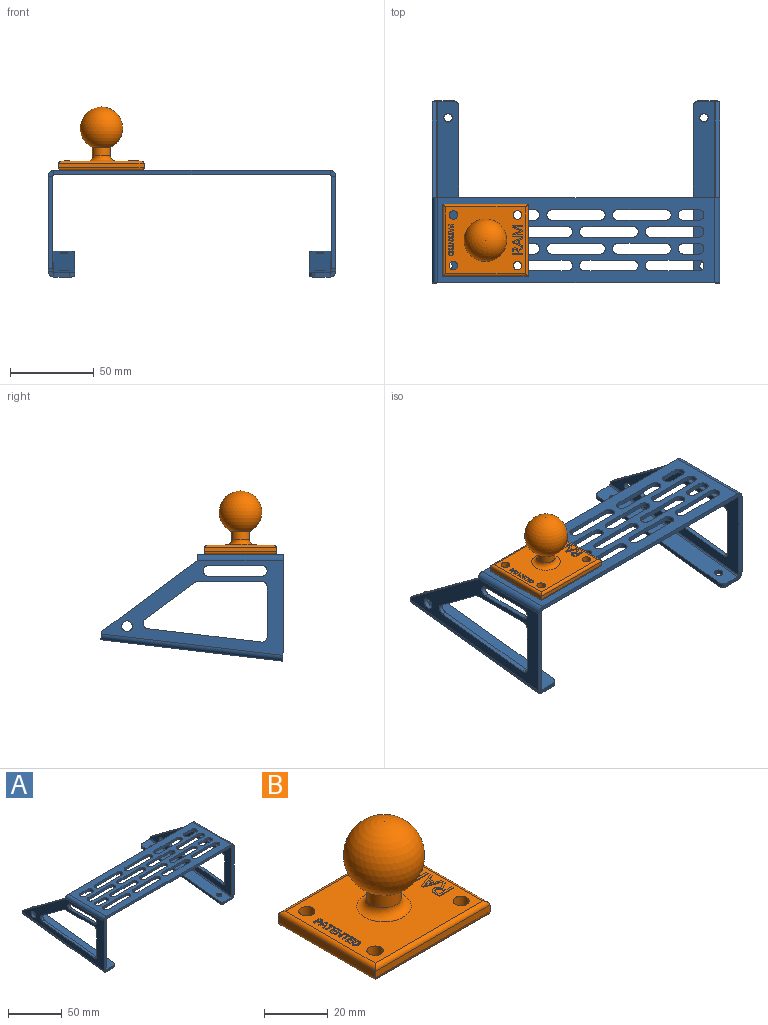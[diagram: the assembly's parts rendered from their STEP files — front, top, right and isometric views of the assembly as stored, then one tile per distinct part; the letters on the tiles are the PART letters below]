
ASSEMBLY  parts=2 mates=1
PART A: 148 faces, bbox 171.5x108.5x63.5 mm
  f0: plane 164.55x2.66mm, normal (0,-1,0), area 437.2mm2, adj f74,f75,f108,f144
  f1: plane 28.58x2.66mm, normal (0,1,0), area 75.9mm2, adj f2,f72,f74,f75
  f2: cylinder r=3.17mm len=6.35mm, axis (0,0,1), area 26.5mm2, adj f1,f3,f74,f75
  f3: plane 28.58x2.66mm, normal (0,-1,0), area 75.9mm2, adj f2,f72,f74,f75
  f4: plane 28.58x2.66mm, normal (0,1,0), area 75.9mm2, adj f5,f71,f74,f75
  f5: cylinder r=3.17mm len=6.35mm, axis (0,0,1), area 26.5mm2, adj f4,f6,f74,f75
  f6: plane 28.58x2.66mm, normal (0,-1,0), area 75.9mm2, adj f5,f71,f74,f75
  f7: plane 28.58x2.66mm, normal (0,1,0), area 75.9mm2, adj f8,f70,f74,f75
  f8: cylinder r=3.17mm len=6.35mm, axis (0,0,1), area 26.5mm2, adj f7,f9,f74,f75
  f9: plane 28.58x2.66mm, normal (0,-1,0), area 75.9mm2, adj f8,f70,f74,f75
  f10: plane 28.58x2.66mm, normal (0,1,0), area 75.9mm2, adj f11,f69,f74,f75
  f11: cylinder r=3.17mm len=6.35mm, axis (0,0,1), area 26.5mm2, adj f10,f12,f74,f75
  f12: plane 28.58x2.66mm, normal (0,-1,0), area 75.9mm2, adj f11,f69,f74,f75
  f13: plane 28.58x2.66mm, normal (0,1,0), area 75.9mm2, adj f14,f68,f74,f75
  f14: cylinder r=3.17mm len=6.35mm, axis (0,0,1), area 26.5mm2, adj f13,f15,f74,f75
  f15: plane 28.58x2.66mm, normal (0,-1,0), area 75.9mm2, adj f14,f68,f74,f75
  f16: plane 28.58x2.66mm, normal (0,1,0), area 75.9mm2, adj f17,f67,f74,f75
  f17: cylinder r=3.17mm len=6.35mm, axis (0,0,1), area 26.5mm2, adj f16,f18,f74,f75
  f18: plane 28.58x2.66mm, normal (0,-1,0), area 75.9mm2, adj f17,f67,f74,f75
  f19: plane 28.58x2.66mm, normal (0,1,0), area 75.9mm2, adj f20,f66,f74,f75
  f20: cylinder r=3.17mm len=6.35mm, axis (0,0,1), area 26.5mm2, adj f19,f21,f74,f75
  f21: plane 28.58x2.66mm, normal (0,-1,0), area 75.9mm2, adj f20,f66,f74,f75
  f22: plane 28.58x2.66mm, normal (0,1,0), area 75.9mm2, adj f23,f65,f74,f75
  f23: cylinder r=3.17mm len=6.35mm, axis (0,0,1), area 26.5mm2, adj f22,f24,f74,f75
  f24: plane 28.58x2.66mm, normal (0,-1,0), area 75.9mm2, adj f23,f65,f74,f75
  f25: cylinder r=3.17mm len=6.35mm, axis (0,0,1), area 26.5mm2, adj f26,f64,f74,f75
  f26: plane 9x2.66mm, normal (0,1,0), area 23.9mm2, adj f25,f27,f74,f75
  f27: cylinder r=3.17mm len=6.35mm, axis (0,0,1), area 26.5mm2, adj f26,f64,f74,f75
  f28: cylinder r=3.17mm len=6.35mm, axis (0,0,1), area 26.5mm2, adj f29,f63,f74,f75
  f29: plane 9x2.66mm, normal (0,-1,0), area 23.9mm2, adj f28,f30,f74,f75
  f30: cylinder r=3.17mm len=6.35mm, axis (0,0,1), area 26.5mm2, adj f29,f63,f74,f75
  f31: cylinder r=3.17mm len=6.35mm, axis (0,0,1), area 26.5mm2, adj f32,f62,f74,f75
  f32: plane 28.58x2.66mm, normal (0,-1,0), area 75.9mm2, adj f31,f33,f74,f75
  f33: cylinder r=3.17mm len=6.35mm, axis (0,0,1), area 26.5mm2, adj f32,f62,f74,f75
  f34: cylinder r=3.17mm len=6.35mm, axis (0,0,1), area 26.5mm2, adj f35,f61,f74,f75
  f35: plane 28.58x2.66mm, normal (0,-1,0), area 75.9mm2, adj f34,f36,f74,f75
  f36: cylinder r=3.17mm len=6.35mm, axis (0,0,1), area 26.5mm2, adj f35,f61,f74,f75
  f37: cylinder r=3.17mm len=6.35mm, axis (0,0,1), area 26.5mm2, adj f38,f60,f74,f75
  f38: plane 28.58x2.66mm, normal (0,-1,0), area 75.9mm2, adj f37,f39,f74,f75
  f39: cylinder r=3.17mm len=6.35mm, axis (0,0,1), area 26.5mm2, adj f38,f60,f74,f75
  f40: cylinder r=3.17mm len=6.35mm, axis (0,0,1), area 26.5mm2, adj f41,f59,f74,f75
  f41: plane 28.58x2.66mm, normal (0,-1,0), area 75.9mm2, adj f40,f42,f74,f75
  f42: cylinder r=3.17mm len=6.35mm, axis (0,0,1), area 26.5mm2, adj f41,f59,f74,f75
  f43: cylinder r=3.17mm len=6.35mm, axis (0,0,1), area 26.5mm2, adj f44,f58,f74,f75
  f44: plane 28.58x2.66mm, normal (0,-1,0), area 75.9mm2, adj f43,f45,f74,f75
  f45: cylinder r=3.17mm len=6.35mm, axis (0,0,1), area 26.5mm2, adj f44,f58,f74,f75
  f46: cylinder r=3.17mm len=6.35mm, axis (0,0,1), area 26.5mm2, adj f47,f57,f74,f75
  f47: plane 28.58x2.66mm, normal (0,-1,0), area 75.9mm2, adj f46,f48,f74,f75
  f48: cylinder r=3.17mm len=6.35mm, axis (0,0,1), area 26.5mm2, adj f47,f57,f74,f75
  f49: cylinder r=3.17mm len=6.35mm, axis (0,0,1), area 26.5mm2, adj f50,f56,f74,f75
  f50: plane 9x2.66mm, normal (0,-1,0), area 23.9mm2, adj f49,f51,f74,f75
  f51: cylinder r=3.17mm len=6.35mm, axis (0,0,1), area 26.5mm2, adj f50,f56,f74,f75
  f52: cylinder r=3.17mm len=6.35mm, axis (0,0,1), area 26.5mm2, adj f53,f55,f74,f75
  f53: plane 9x2.66mm, normal (0,1,0), area 23.9mm2, adj f52,f54,f74,f75
  f54: cylinder r=3.17mm len=6.35mm, axis (0,0,1), area 26.5mm2, adj f53,f55,f74,f75
  f55: plane 9x2.66mm, normal (0,-1,0), area 23.9mm2, adj f52,f54,f74,f75
  f56: plane 9x2.66mm, normal (0,1,0), area 23.9mm2, adj f49,f51,f74,f75
  f57: plane 28.58x2.66mm, normal (0,1,0), area 75.9mm2, adj f46,f48,f74,f75
  f58: plane 28.58x2.66mm, normal (0,1,0), area 75.9mm2, adj f43,f45,f74,f75
  f59: plane 28.58x2.66mm, normal (0,1,0), area 75.9mm2, adj f40,f42,f74,f75
  f60: plane 28.58x2.66mm, normal (0,1,0), area 75.9mm2, adj f37,f39,f74,f75
  f61: plane 28.58x2.66mm, normal (0,1,0), area 75.9mm2, adj f34,f36,f74,f75
  f62: plane 28.58x2.66mm, normal (0,1,0), area 75.9mm2, adj f31,f33,f74,f75
  f63: plane 9x2.66mm, normal (0,1,0), area 23.9mm2, adj f28,f30,f74,f75
  f64: plane 9x2.66mm, normal (0,-1,0), area 23.9mm2, adj f25,f27,f74,f75
  f65: cylinder r=3.17mm len=6.35mm, axis (0,0,1), area 26.5mm2, adj f22,f24,f74,f75
  f66: cylinder r=3.17mm len=6.35mm, axis (0,0,1), area 26.5mm2, adj f19,f21,f74,f75
  f67: cylinder r=3.17mm len=6.35mm, axis (0,0,1), area 26.5mm2, adj f16,f18,f74,f75
  f68: cylinder r=3.17mm len=6.35mm, axis (0,0,1), area 26.5mm2, adj f13,f15,f74,f75
  f69: cylinder r=3.17mm len=6.35mm, axis (0,0,1), area 26.5mm2, adj f10,f12,f74,f75
  f70: cylinder r=3.17mm len=6.35mm, axis (0,0,1), area 26.5mm2, adj f7,f9,f74,f75
  f71: cylinder r=3.17mm len=6.35mm, axis (0,0,1), area 26.5mm2, adj f4,f6,f74,f75
  f72: cylinder r=3.17mm len=6.35mm, axis (0,0,1), area 26.5mm2, adj f1,f3,f74,f75
  f73: plane 164.55x2.66mm, normal (0,1,0), area 437.2mm2, adj f74,f75,f109,f145
  f74: plane 164.55x50.8mm, normal (0,0,-1), area 5020.2mm2, adj f0,f1,f2,f3,f4,f5,f6,f7
  f75: plane 164.55x50.8mm, normal (0,0,1), area 5020.2mm2, adj f0,f1,f2,f3,f4,f5,f6,f7
  f76: cylinder r=3.17mm len=6.35mm, axis (-1,0,0), area 26.5mm2, adj f77,f89,f90,f91
  f77: plane 31.75x2.66mm, normal (0,0,1), area 84.4mm2, adj f76,f78,f90,f91
  f78: cylinder r=3.17mm len=6.35mm, axis (-1,0,0), area 26.5mm2, adj f77,f89,f90,f91
  f79: plane 54.97x2.66mm, normal (0,-1,0), area 146mm2, adj f88,f90,f91,f108
  f80: plane 57.15x42.27mm, normal (0,0.59,0.8), area 188.9mm2, adj f81,f90,f91,f109
  f81: plane 2.66x1.62mm, normal (0,0.99,0.12), area 4.3mm2, adj f80,f90,f91,f105
  f82: plane 29.65x2.66mm, normal (0,1,0), area 78.8mm2, adj f90,f91,f92,f94
  f83: plane 67.55x7.95mm, normal (0,-0.12,0.99), area 180.7mm2, adj f84,f90,f91,f92
  f84: cylinder r=3.17mm len=5.71mm, axis (-1,0,0), area 20.1mm2, adj f83,f85,f90,f91
  f85: plane 29.34x21.7mm, normal (0,-0.59,-0.8), area 97mm2, adj f84,f90,f91,f93
  f86: cylinder r=3.17mm len=6.35mm, axis (-1,0,0), area 53mm2, adj f90,f91
  f87: plane 38.21x2.66mm, normal (0,0,-1), area 101.5mm2, adj f90,f91,f93,f94
  f88: plane 2.66x1.62mm, normal (0,-0.99,-0.12), area 4.3mm2, adj f79,f90,f91,f104
  f89: plane 31.75x2.66mm, normal (0,0,-1), area 84.4mm2, adj f76,f78,f90,f91
  f90: plane 108.14x56.59mm, normal (-1,0,0), area 1957.8mm2, adj f76,f77,f78,f79,f80,f81,f82,f83
  f91: plane 108.14x56.59mm, normal (1,0,0), area 1957.8mm2, adj f76,f77,f78,f79,f80,f81,f82,f83
  f92: cylinder r=3.17mm len=3.55mm, axis (1,0,0), area 14.2mm2, adj f82,f83,f90,f91
  f93: cylinder r=3.17mm len=2.66mm, axis (1,0,0), area 5.4mm2, adj f85,f87,f90,f91
  f94: cylinder r=3.17mm len=3.18mm, axis (1,0,0), area 13.3mm2, adj f82,f87,f90,f91
  f95: plane 101.95x14.6mm, normal (-1,0,0), area 271.9mm2, adj f100,f101,f102,f103
  f96: plane 9.25x2.64mm, normal (0,-0.99,-0.12), area 24.6mm2, adj f100,f101,f102,f104
  f97: cylinder r=2.54mm len=5.36mm, axis (0,-0.12,0.99), area 42.4mm2, adj f100,f101
  f98: cylinder r=2.54mm len=5.36mm, axis (0,-0.12,0.99), area 42.4mm2, adj f100,f101
  f99: plane 9.25x2.64mm, normal (0,0.99,0.12), area 24.6mm2, adj f100,f101,f103,f105
  f100: plane 107.95x12.7mm, normal (0,-0.12,0.99), area 1305.6mm2, adj f95,f96,f97,f98,f99,f102,f103,f107
  f101: plane 107.95x12.7mm, normal (0,0.12,-0.99), area 1305.6mm2, adj f95,f96,f97,f98,f99,f102,f103,f106
  f102: cylinder r=3.17mm len=3.46mm, axis (0,-0.12,0.99), area 13.3mm2, adj f95,f96,f100,f101
  f103: cylinder r=3.17mm len=3.46mm, axis (0,-0.12,0.99), area 13.3mm2, adj f95,f99,f100,f101
  f104: plane 3.45x3.43mm, normal (0,-0.99,-0.12), area 8.9mm2, adj f88,f96,f106,f107
  f105: plane 3.45x3.43mm, normal (0,0.99,0.12), area 8.9mm2, adj f81,f99,f106,f107
  f106: cylinder r=3.45mm len=108.35mm, axis (0,-0.99,-0.12), area 589.1mm2, adj f91,f101,f104,f105
  f107: cylinder r=0.79mm len=108.04mm, axis (0,-0.99,-0.12), area 135.5mm2, adj f90,f100,f104,f105
  f108: plane 3.45x3.45mm, normal (0,-1,0), area 8.9mm2, adj f0,f79,f110,f111
  f109: plane 3.45x3.45mm, normal (0,1,0), area 8.9mm2, adj f73,f80,f110,f111
  f110: cylinder r=3.45mm len=50.8mm, axis (0,-1,0), area 275.3mm2, adj f75,f91,f108,f109
  f111: cylinder r=0.79mm len=50.8mm, axis (0,-1,0), area 63.3mm2, adj f74,f90,f108,f109
  f112: cylinder r=3.17mm len=6.35mm, axis (1,0,0), area 26.5mm2, adj f113,f125,f126,f127
  f113: plane 31.75x2.66mm, normal (0,0,1), area 84.4mm2, adj f112,f114,f126,f127
  f114: cylinder r=3.17mm len=6.35mm, axis (1,0,0), area 26.5mm2, adj f113,f125,f126,f127
  f115: plane 54.97x2.66mm, normal (0,-1,0), area 146mm2, adj f116,f126,f127,f144
  f116: plane 2.66x1.62mm, normal (0,-0.99,-0.12), area 4.3mm2, adj f115,f126,f127,f141
  f117: plane 2.66x1.62mm, normal (0,0.99,0.12), area 4.3mm2, adj f118,f126,f127,f140
  f118: plane 57.15x42.27mm, normal (0,0.59,0.8), area 188.9mm2, adj f117,f126,f127,f145
  f119: plane 67.55x7.95mm, normal (0,-0.12,0.99), area 180.7mm2, adj f124,f126,f127,f129
  f120: plane 29.65x2.66mm, normal (0,1,0), area 78.8mm2, adj f126,f127,f128,f129
  f121: plane 38.21x2.66mm, normal (0,0,-1), area 101.5mm2, adj f126,f127,f128,f130
  f122: plane 29.34x21.7mm, normal (0,-0.59,-0.8), area 97mm2, adj f124,f126,f127,f130
  f123: cylinder r=3.17mm len=6.35mm, axis (1,0,0), area 53mm2, adj f126,f127
  f124: cylinder r=3.17mm len=5.71mm, axis (1,0,0), area 20.1mm2, adj f119,f122,f126,f127
  f125: plane 31.75x2.66mm, normal (0,0,-1), area 84.4mm2, adj f112,f114,f126,f127
  f126: plane 108.14x56.59mm, normal (1,0,0), area 1957.8mm2, adj f112,f113,f114,f115,f116,f117,f118,f119
  f127: plane 108.14x56.59mm, normal (-1,0,0), area 1957.8mm2, adj f112,f113,f114,f115,f116,f117,f118,f119
  f128: cylinder r=3.17mm len=3.18mm, axis (-1,0,0), area 13.3mm2, adj f120,f121,f126,f127
  f129: cylinder r=3.17mm len=3.55mm, axis (-1,0,0), area 14.2mm2, adj f119,f120,f126,f127
  f130: cylinder r=3.17mm len=2.66mm, axis (-1,0,0), area 5.4mm2, adj f121,f122,f126,f127
  f131: plane 101.95x14.6mm, normal (1,0,0), area 271.9mm2, adj f136,f137,f138,f139
  f132: plane 9.25x2.64mm, normal (0,0.99,0.12), area 24.6mm2, adj f136,f137,f139,f140
  f133: cylinder r=2.54mm len=5.36mm, axis (0,-0.12,0.99), area 42.4mm2, adj f136,f137
  f134: cylinder r=2.54mm len=5.36mm, axis (0,-0.12,0.99), area 42.4mm2, adj f136,f137
  f135: plane 9.25x2.64mm, normal (0,-0.99,-0.12), area 24.6mm2, adj f136,f137,f138,f141
  f136: plane 107.95x12.7mm, normal (0,-0.12,0.99), area 1305.6mm2, adj f131,f132,f133,f134,f135,f138,f139,f143
  f137: plane 107.95x12.7mm, normal (0,0.12,-0.99), area 1305.6mm2, adj f131,f132,f133,f134,f135,f138,f139,f142
  f138: cylinder r=3.17mm len=3.46mm, axis (0,-0.12,0.99), area 13.3mm2, adj f131,f135,f136,f137
  f139: cylinder r=3.17mm len=3.46mm, axis (0,-0.12,0.99), area 13.3mm2, adj f131,f132,f136,f137
  f140: plane 3.45x3.43mm, normal (0,0.99,0.12), area 8.9mm2, adj f117,f132,f142,f143
  f141: plane 3.45x3.43mm, normal (0,-0.99,-0.12), area 8.9mm2, adj f116,f135,f142,f143
  f142: cylinder r=3.45mm len=108.35mm, axis (0,0.99,0.12), area 589.1mm2, adj f127,f137,f140,f141
  f143: cylinder r=0.79mm len=108.04mm, axis (0,0.99,0.12), area 135.5mm2, adj f126,f136,f140,f141
  f144: plane 3.45x3.45mm, normal (0,-1,0), area 8.9mm2, adj f0,f115,f146,f147
  f145: plane 3.45x3.45mm, normal (0,1,0), area 8.9mm2, adj f73,f118,f146,f147
  f146: cylinder r=3.45mm len=50.8mm, axis (0,-1,0), area 275.3mm2, adj f75,f127,f144,f145
  f147: cylinder r=0.79mm len=50.8mm, axis (0,-1,0), area 63.3mm2, adj f74,f126,f144,f145
PART B: 183 faces, bbox 50.8x42.9x37.8 mm
  f0: plane 47.63x39.75mm, normal (0,0,1), area 1517.2mm2, adj f8,f13,f14,f15,f16,f17,f18,f19
  f1: plane 42.93x2.41mm, normal (1,0,0), area 103.6mm2, adj f2,f4,f9,f13
  f2: plane 50.8x2.41mm, normal (0,1,0), area 122.6mm2, adj f1,f3,f10,f14
  f3: plane 42.93x2.41mm, normal (-1,0,0), area 103.6mm2, adj f2,f4,f12,f16
  f4: plane 50.8x2.41mm, normal (0,-1,0), area 122.6mm2, adj f1,f3,f11,f15
  f5: plane 47.63x39.75mm, normal (0,0,-1), area 1812.1mm2, adj f9,f10,f11,f12,f17,f18,f19,f20
  f6: cylinder r=5.33mm len=10.67mm, axis (0,0,-1), area 162.8mm2, adj f7,f8
  f7: sphere r=12.7mm, area 1933.1mm2, adj f6
  f8: torus R=8.51mm, axis (0,0,1), area 203.3mm2, adj f0,f6
  f9: cylinder r=1.59mm len=42.93mm, axis (0,1,0), area 104.2mm2, adj f1,f5,f10,f11
  f10: cylinder r=1.59mm len=50.8mm, axis (-1,0,0), area 123.8mm2, adj f2,f5,f9,f12
  f11: cylinder r=1.59mm len=50.8mm, axis (1,0,0), area 123.8mm2, adj f4,f5,f9,f12
  f12: cylinder r=1.59mm len=42.93mm, axis (0,-1,0), area 104.2mm2, adj f3,f5,f10,f11
  f13: cylinder r=1.59mm len=42.93mm, axis (0,-1,0), area 104.2mm2, adj f0,f1,f14,f15
  f14: cylinder r=1.59mm len=50.8mm, axis (1,0,0), area 123.8mm2, adj f0,f2,f13,f16
  f15: cylinder r=1.59mm len=50.8mm, axis (-1,0,0), area 123.8mm2, adj f0,f4,f13,f16
  f16: cylinder r=1.59mm len=42.93mm, axis (0,1,0), area 104.2mm2, adj f0,f3,f14,f15
  f17: cylinder r=2.54mm len=5.59mm, axis (0,0,1), area 89.2mm2, adj f0,f5
  f18: cylinder r=2.54mm len=5.59mm, axis (0,0,1), area 89.2mm2, adj f0,f5
  f19: cylinder r=2.54mm len=5.59mm, axis (0,0,1), area 89.2mm2, adj f0,f5
  f20: cylinder r=2.54mm len=5.59mm, axis (0,0,1), area 89.2mm2, adj f0,f5
  f21: plane 1x0.25mm, normal (-1,0,0), area 0.3mm2, adj f22,f38,f39,f40
  f22: plane 2.41x0.25mm, normal (0,1,0), area 0.6mm2, adj f21,f23,f39,f40
  f23: plane 0.95x0.25mm, normal (1,0,0), area 0.2mm2, adj f22,f24,f39,f40
  f24: extruded ~1.18x0.28mm, area 0.3mm2, adj f23,f25,f39,f40
  f25: extruded ~0.9x0.37mm, area 0.3mm2, adj f24,f26,f39,f40
  f26: extruded ~0.92x0.36mm, area 0.3mm2, adj f25,f38,f39,f40
  f27: plane 2.62x0.25mm, normal (0,1,0), area 0.7mm2, adj f0,f28,f37,f39
  f28: plane 1.31x0.25mm, normal (1,0,0), area 0.3mm2, adj f0,f27,f29,f39
  f29: plane 2.62x1.52mm, normal (0.5,-0.86,0), area 0.8mm2, adj f0,f28,f30,f39
  f30: plane 0.87x0.25mm, normal (1,0,0), area 0.2mm2, adj f0,f29,f31,f39
  f31: plane 2.83x1.71mm, normal (-0.52,0.86,0), area 0.8mm2, adj f0,f30,f32,f39
  f32: extruded ~1.69x1.27mm, area 0.6mm2, adj f0,f31,f33,f39
  f33: extruded ~1.34x0.55mm, area 0.4mm2, adj f0,f32,f34,f39
  f34: extruded ~1.71x0.44mm, area 0.5mm2, adj f0,f33,f35,f39
  f35: plane 1.73x0.25mm, normal (-1,0,0), area 0.4mm2, adj f0,f34,f36,f39
  f36: plane 6.3x0.25mm, normal (0,-1,0), area 1.6mm2, adj f0,f35,f37,f39
  f37: plane 0.73x0.25mm, normal (1,0,0), area 0.2mm2, adj f0,f27,f36,f39
  f38: extruded ~1.14x0.31mm, area 0.3mm2, adj f21,f26,f39,f40
  f39: plane 6.3x4.44mm, normal (0,0,1), area 11.9mm2, adj f21,f22,f23,f24,f25,f26,f27,f28
  f40: plane 2.5x2.41mm, normal (0,0,1), area 5.4mm2, adj f21,f22,f23,f24,f25,f26,f38
  f41: plane 1.95x0.73mm, normal (0.35,-0.94,0), area 0.5mm2, adj f42,f53,f54,f55
  f42: plane 2.04x0.25mm, normal (-1,0,0), area 0.5mm2, adj f41,f43,f54,f55
  f43: plane 1.95x0.74mm, normal (0.35,0.94,0), area 0.5mm2, adj f42,f44,f54,f55
  f44: extruded ~0.91x0.27mm, area 0.2mm2, adj f43,f53,f54,f55
  f45: plane 2x0.78mm, normal (0.36,-0.93,0), area 0.5mm2, adj f0,f46,f52,f54
  f46: plane 0.76x0.25mm, normal (1,0,0), area 0.2mm2, adj f0,f45,f47,f54
  f47: plane 6.32x2.48mm, normal (-0.36,0.93,0), area 1.7mm2, adj f0,f46,f48,f54
  f48: plane 0.62x0.25mm, normal (-1,0,0), area 0.2mm2, adj f0,f47,f49,f54
  f49: plane 6.32x2.49mm, normal (-0.37,-0.93,0), area 1.7mm2, adj f0,f48,f50,f54
  f50: plane 0.74x0.25mm, normal (1,0,0), area 0.2mm2, adj f0,f49,f51,f54
  f51: plane 2x0.77mm, normal (0.36,0.93,0), area 0.5mm2, adj f0,f50,f52,f54
  f52: plane 2.52x0.25mm, normal (1,0,0), area 0.6mm2, adj f0,f45,f51,f54
  f53: extruded ~0.91x0.29mm, area 0.2mm2, adj f41,f44,f54,f55
  f54: plane 6.32x5.58mm, normal (0,0,1), area 10.2mm2, adj f41,f42,f43,f44,f45,f46,f47,f48
  f55: plane 2.86x2.04mm, normal (0,0,1), area 2.8mm2, adj f41,f42,f43,f44,f53
  f56: plane 5.58x2.14mm, normal (0.36,-0.93,0), area 1.5mm2, adj f0,f57,f73,f74
  f57: plane 0.59x0.25mm, normal (1,0,0), area 0.1mm2, adj f0,f56,f58,f74
  f58: plane 5.57x2.15mm, normal (0.36,0.93,0), area 1.5mm2, adj f0,f57,f59,f74
  f59: plane 0.25x0.03mm, normal (1,0,0), area 0mm2, adj f0,f58,f60,f74
  f60: extruded ~1.52x0.25mm, area 0.4mm2, adj f0,f59,f61,f74
  f61: plane 4.06x0.25mm, normal (0,-1,0), area 1mm2, adj f0,f60,f62,f74
  f62: plane 0.73x0.25mm, normal (1,0,0), area 0.2mm2, adj f0,f61,f63,f74
  f63: plane 6.3x0.25mm, normal (0,1,0), area 1.6mm2, adj f0,f62,f64,f74
  f64: plane 1.09x0.25mm, normal (-1,0,0), area 0.3mm2, adj f0,f63,f65,f74
  f65: plane 5.19x2.01mm, normal (-0.36,-0.93,0), area 1.4mm2, adj f0,f64,f66,f74
  f66: plane 0.25x0.03mm, normal (-1,0,0), area 0mm2, adj f0,f65,f67,f74
  f67: plane 5.19x1.99mm, normal (-0.36,0.93,0), area 1.4mm2, adj f0,f66,f68,f74
  f68: plane 1.1x0.25mm, normal (-1,0,0), area 0.3mm2, adj f0,f67,f69,f74
  f69: plane 6.3x0.25mm, normal (0,-1,0), area 1.6mm2, adj f0,f68,f70,f74
  f70: plane 0.68x0.25mm, normal (1,0,0), area 0.2mm2, adj f0,f69,f71,f74
  f71: plane 4x0.25mm, normal (0,1,0), area 1mm2, adj f0,f70,f72,f74
  f72: extruded ~1.58x0.25mm, area 0.4mm2, adj f0,f71,f73,f74
  f73: plane 0.25x0.03mm, normal (1,0,0), area 0mm2, adj f0,f56,f72,f74
  f74: plane 6.3x6.24mm, normal (0,0,1), area 17mm2, adj f56,f57,f58,f59,f60,f61,f62,f63
  f75: plane 0.29x0.25mm, normal (1,0,0), area 0.1mm2, adj f76,f89,f90,f91
  f76: plane 1.13x0.25mm, normal (0,-1,0), area 0.3mm2, adj f75,f77,f90,f91
  f77: plane 0.36x0.25mm, normal (-1,0,0), area 0.1mm2, adj f76,f78,f90,f91
  f78: extruded ~0.56x0.25mm, area 0.1mm2, adj f77,f79,f90,f91
  f79: extruded ~0.41x0.25mm, area 0.1mm2, adj f78,f80,f90,f91
  f80: extruded ~0.44x0.25mm, area 0.1mm2, adj f79,f89,f90,f91
  f81: extruded ~0.65x0.29mm, area 0.2mm2, adj f0,f82,f88,f90
  f82: extruded ~1.04x0.81mm, area 0.4mm2, adj f0,f81,f83,f90
  f83: plane 0.72x0.25mm, normal (1,0,0), area 0.2mm2, adj f0,f82,f84,f90
  f84: plane 2.77x0.25mm, normal (0,1,0), area 0.7mm2, adj f0,f83,f85,f90
  f85: plane 0.32x0.25mm, normal (-1,0,0), area 0.1mm2, adj f0,f84,f86,f90
  f86: plane 1.09x0.25mm, normal (0,-1,0), area 0.3mm2, adj f0,f85,f87,f90
  f87: plane 0.33x0.25mm, normal (-1,0,0), area 0.1mm2, adj f0,f86,f88,f90
  f88: extruded ~0.82x0.25mm, area 0.2mm2, adj f0,f81,f87,f90
  f89: extruded ~0.62x0.25mm, area 0.2mm2, adj f75,f80,f90,f91
  f90: plane 2.77x1.76mm, normal (0,0,1), area 1.9mm2, adj f75,f76,f77,f78,f79,f80,f81,f82
  f91: plane 1.13x1.1mm, normal (0,0,1), area 1.1mm2, adj f75,f76,f77,f78,f79,f80,f89
  f92: plane 0.86x0.32mm, normal (-0.35,0.94,0), area 0.2mm2, adj f93,f104,f105,f106
  f93: plane 0.9x0.25mm, normal (1,0,0), area 0.2mm2, adj f92,f94,f105,f106
  f94: plane 0.86x0.33mm, normal (-0.35,-0.94,0), area 0.2mm2, adj f93,f95,f105,f106
  f95: extruded ~0.4x0.25mm, area 0.1mm2, adj f94,f104,f105,f106
  f96: plane 0.88x0.35mm, normal (-0.36,0.93,0), area 0.2mm2, adj f0,f97,f103,f105
  f97: plane 0.33x0.25mm, normal (-1,0,0), area 0.1mm2, adj f0,f96,f98,f105
  f98: plane 2.78x1.09mm, normal (0.36,-0.93,0), area 0.8mm2, adj f0,f97,f99,f105
  f99: plane 0.27x0.25mm, normal (1,0,0), area 0.1mm2, adj f0,f98,f100,f105
  f100: plane 2.78x1.1mm, normal (0.37,0.93,0), area 0.8mm2, adj f0,f99,f101,f105
  f101: plane 0.33x0.25mm, normal (-1,0,0), area 0.1mm2, adj f0,f100,f102,f105
  f102: plane 0.88x0.34mm, normal (-0.36,-0.93,0), area 0.2mm2, adj f0,f101,f103,f105
  f103: plane 1.11x0.25mm, normal (-1,0,0), area 0.3mm2, adj f0,f96,f102,f105
  f104: extruded ~0.4x0.25mm, area 0.1mm2, adj f92,f95,f105,f106
  f105: plane 2.78x2.46mm, normal (0,0,1), area 2mm2, adj f92,f93,f94,f95,f96,f97,f98,f99
  f106: plane 1.26x0.9mm, normal (0,0,1), area 0.5mm2, adj f92,f93,f94,f95,f104
  f107: plane 0.32x0.25mm, normal (-1,0,0), area 0.1mm2, adj f0,f108,f114,f115
  f108: plane 2.48x0.25mm, normal (0,-1,0), area 0.6mm2, adj f0,f107,f109,f115
  f109: plane 0.88x0.25mm, normal (-1,0,0), area 0.2mm2, adj f0,f108,f110,f115
  f110: plane 0.29x0.25mm, normal (0,-1,0), area 0.1mm2, adj f0,f109,f111,f115
  f111: plane 2.08x0.25mm, normal (1,0,0), area 0.5mm2, adj f0,f110,f112,f115
  f112: plane 0.29x0.25mm, normal (0,1,0), area 0.1mm2, adj f0,f111,f113,f115
  f113: plane 0.88x0.25mm, normal (-1,0,0), area 0.2mm2, adj f0,f112,f114,f115
  f114: plane 2.48x0.25mm, normal (0,1,0), area 0.6mm2, adj f0,f107,f113,f115
  f115: plane 2.77x2.08mm, normal (0,0,1), area 1.4mm2, adj f107,f108,f109,f110,f111,f112,f113,f114
  f116: plane 1.54x0.25mm, normal (-1,0,0), area 0.4mm2, adj f0,f117,f127,f128
  f117: plane 0.29x0.25mm, normal (0,-1,0), area 0.1mm2, adj f0,f116,f118,f128
  f118: plane 1.22x0.25mm, normal (1,0,0), area 0.3mm2, adj f0,f117,f119,f128
  f119: plane 1.02x0.25mm, normal (0,-1,0), area 0.3mm2, adj f0,f118,f120,f128
  f120: plane 1.15x0.25mm, normal (-1,0,0), area 0.3mm2, adj f0,f119,f121,f128
  f121: plane 0.28x0.25mm, normal (0,-1,0), area 0.1mm2, adj f0,f120,f122,f128
  f122: plane 1.15x0.25mm, normal (1,0,0), area 0.3mm2, adj f0,f121,f123,f128
  f123: plane 0.89x0.25mm, normal (0,-1,0), area 0.2mm2, adj f0,f122,f124,f128
  f124: plane 1.22x0.25mm, normal (-1,0,0), area 0.3mm2, adj f0,f123,f125,f128
  f125: plane 0.29x0.25mm, normal (0,-1,0), area 0.1mm2, adj f0,f124,f126,f128
  f126: plane 1.54x0.25mm, normal (1,0,0), area 0.4mm2, adj f0,f125,f127,f128
  f127: plane 2.77x0.25mm, normal (0,1,0), area 0.7mm2, adj f0,f116,f126,f128
  f128: plane 2.77x1.54mm, normal (0,0,1), area 1.9mm2, adj f116,f117,f118,f119,f120,f121,f122,f123
  f129: plane 0.37x0.25mm, normal (-1,0,0), area 0.1mm2, adj f0,f130,f143,f144
  f130: plane 2.77x0.25mm, normal (0,-1,0), area 0.7mm2, adj f0,f129,f131,f144
  f131: plane 0.3x0.25mm, normal (1,0,0), area 0.1mm2, adj f0,f130,f132,f144
  f132: plane 1.59x0.25mm, normal (0,1,0), area 0.4mm2, adj f0,f131,f133,f144
  f133: extruded ~0.4x0.25mm, area 0.1mm2, adj f0,f132,f134,f144
  f134: extruded ~0.33x0.25mm, area 0.1mm2, adj f0,f133,f135,f144
  f135: plane 0.25x0.02mm, normal (1,0,0), area 0mm2, adj f0,f134,f136,f144
  f136: plane 2.32x1.51mm, normal (0.55,-0.84,0), area 0.7mm2, adj f0,f135,f137,f144
  f137: plane 0.36x0.25mm, normal (1,0,0), area 0.1mm2, adj f0,f136,f138,f144
  f138: plane 2.77x0.25mm, normal (0,1,0), area 0.7mm2, adj f0,f137,f139,f144
  f139: plane 0.3x0.25mm, normal (-1,0,0), area 0.1mm2, adj f0,f138,f140,f144
  f140: plane 1.57x0.25mm, normal (0,-1,0), area 0.4mm2, adj f0,f139,f141,f144
  f141: extruded ~0.75x0.25mm, area 0.2mm2, adj f0,f140,f142,f144
  f142: plane 0.25x0.02mm, normal (-1,0,0), area 0mm2, adj f0,f141,f143,f144
  f143: plane 2.32x1.51mm, normal (-0.55,0.84,0), area 0.7mm2, adj f0,f129,f142,f144
  f144: plane 2.77x2.16mm, normal (0,0,1), area 2.5mm2, adj f129,f130,f131,f132,f133,f134,f135,f136
  f145: plane 0.32x0.25mm, normal (-1,0,0), area 0.1mm2, adj f0,f146,f152,f153
  f146: plane 2.48x0.25mm, normal (0,-1,0), area 0.6mm2, adj f0,f145,f147,f153
  f147: plane 0.88x0.25mm, normal (-1,0,0), area 0.2mm2, adj f0,f146,f148,f153
  f148: plane 0.29x0.25mm, normal (0,-1,0), area 0.1mm2, adj f0,f147,f149,f153
  f149: plane 2.08x0.25mm, normal (1,0,0), area 0.5mm2, adj f0,f148,f150,f153
  f150: plane 0.29x0.25mm, normal (0,1,0), area 0.1mm2, adj f0,f149,f151,f153
  f151: plane 0.88x0.25mm, normal (-1,0,0), area 0.2mm2, adj f0,f150,f152,f153
  f152: plane 2.48x0.25mm, normal (0,1,0), area 0.6mm2, adj f0,f145,f151,f153
  f153: plane 2.77x2.08mm, normal (0,0,1), area 1.4mm2, adj f145,f146,f147,f148,f149,f150,f151,f152
  f154: plane 1.54x0.25mm, normal (-1,0,0), area 0.4mm2, adj f0,f155,f165,f166
  f155: plane 0.29x0.25mm, normal (0,-1,0), area 0.1mm2, adj f0,f154,f156,f166
  f156: plane 1.22x0.25mm, normal (1,0,0), area 0.3mm2, adj f0,f155,f157,f166
  f157: plane 1.02x0.25mm, normal (0,-1,0), area 0.3mm2, adj f0,f156,f158,f166
  f158: plane 1.15x0.25mm, normal (-1,0,0), area 0.3mm2, adj f0,f157,f159,f166
  f159: plane 0.28x0.25mm, normal (0,-1,0), area 0.1mm2, adj f0,f158,f160,f166
  f160: plane 1.15x0.25mm, normal (1,0,0), area 0.3mm2, adj f0,f159,f161,f166
  f161: plane 0.89x0.25mm, normal (0,-1,0), area 0.2mm2, adj f0,f160,f162,f166
  f162: plane 1.22x0.25mm, normal (-1,0,0), area 0.3mm2, adj f0,f161,f163,f166
  f163: plane 0.29x0.25mm, normal (0,-1,0), area 0.1mm2, adj f0,f162,f164,f166
  f164: plane 1.54x0.25mm, normal (1,0,0), area 0.4mm2, adj f0,f163,f165,f166
  f165: plane 2.77x0.25mm, normal (0,1,0), area 0.7mm2, adj f0,f154,f164,f166
  f166: plane 2.77x1.54mm, normal (0,0,1), area 1.9mm2, adj f154,f155,f156,f157,f158,f159,f160,f161
  f167: extruded ~0.82x0.27mm, area 0.2mm2, adj f168,f180,f181,f182
  f168: extruded ~0.84x0.29mm, area 0.2mm2, adj f167,f169,f181,f182
  f169: extruded ~0.87x0.28mm, area 0.2mm2, adj f168,f170,f181,f182
  f170: plane 0.39x0.25mm, normal (1,0,0), area 0.1mm2, adj f169,f171,f181,f182
  f171: plane 2.21x0.25mm, normal (0,-1,0), area 0.6mm2, adj f170,f172,f181,f182
  f172: plane 0.47x0.25mm, normal (-1,0,0), area 0.1mm2, adj f171,f180,f181,f182
  f173: extruded ~1.05x0.37mm, area 0.3mm2, adj f0,f174,f179,f181
  f174: extruded ~1x0.36mm, area 0.3mm2, adj f0,f173,f175,f181
  f175: extruded ~1x0.36mm, area 0.3mm2, adj f0,f174,f176,f181
  f176: plane 0.85x0.25mm, normal (1,0,0), area 0.2mm2, adj f0,f175,f177,f181
  f177: plane 2.77x0.25mm, normal (0,1,0), area 0.7mm2, adj f0,f176,f178,f181
  f178: plane 0.77x0.25mm, normal (-1,0,0), area 0.2mm2, adj f0,f177,f179,f181
  f179: extruded ~1.07x0.36mm, area 0.3mm2, adj f0,f173,f178,f181
  f180: extruded ~0.81x0.27mm, area 0.2mm2, adj f167,f172,f181,f182
  f181: plane 2.77x2.21mm, normal (0,0,1), area 2.4mm2, adj f167,f168,f169,f170,f171,f172,f173,f174
  f182: plane 2.21x1.55mm, normal (0,0,1), area 3mm2, adj f167,f168,f169,f170,f171,f172,f180
PLACE A t=(-0.05,-0.91,34.12)mm
PLACE B t=(-54.03,-32.66,36.78)mm
MATE fastened B.f20 <-> A.f69  axis (0,0,-1) through (-73.08,-47.74,36.78)mm
